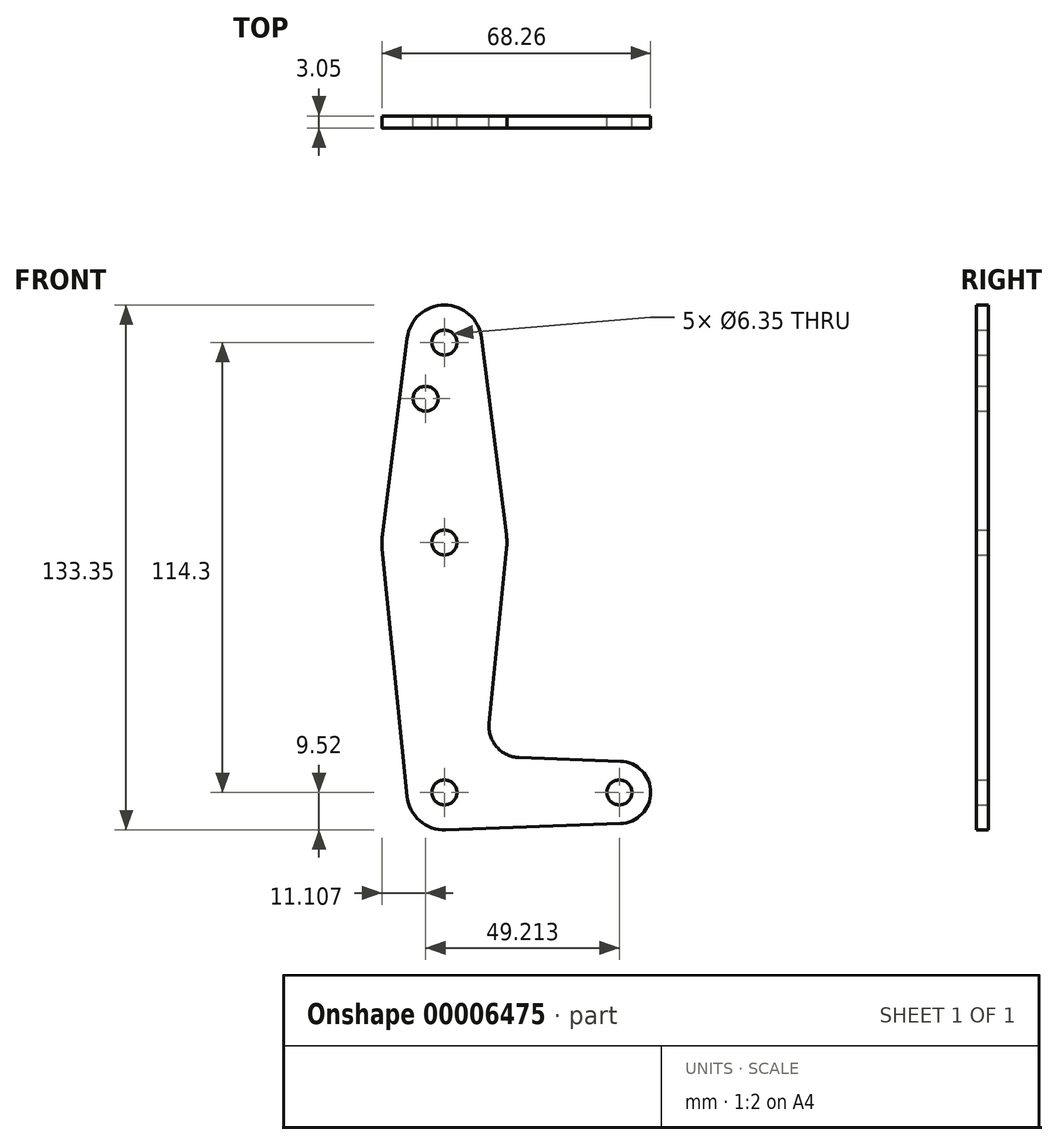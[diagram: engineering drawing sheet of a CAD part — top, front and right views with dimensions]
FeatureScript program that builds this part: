
annotation { "Feature Type Name" : "Feature", "Feature Type Description" : "" }
export const myFeature = defineFeature(function(context is Context, id is Id, definition is map)
    precondition{}
    {
        {
            var Q0;
            Q0=qCreatedBy(makeId("Front.planeOp"),FACE);
            var sketch = newSketch(context, id + "F0", { "sketchPlane" : qUnion([Q0])});
            skLineSegment(sketch, "E0", {"start": v(0, 114.3) * mm, "end": v(0, 0) * mm, "construction": true});
            skLineSegment(sketch, "E1", {"start": v(0, 0) * mm, "end": v(44.45, 0) * mm, "construction": true});
            skCircle(sketch, "E2", {"center": v(0, 0) * mm, "radius": 9.53 * mm});
            skCircle(sketch, "E3", {"center": v(0, 63.5) * mm, "radius": 15.88 * mm});
            skCircle(sketch, "E4", {"center": v(0, 114.3) * mm, "radius": 9.53 * mm});
            skCircle(sketch, "E5", {"center": v(44.45, 0) * mm, "radius": 7.94 * mm});
            skLineSegment(sketch, "E6", {"start": v(-9.45, 115.5) * mm, "end": v(-15.75, 65.48) * mm});
            skLineSegment(sketch, "E7", {"start": v(11.37, 17.59) * mm, "end": v(15.8, 61.92) * mm});
            skLineSegment(sketch, "E8", {"start": v(15.75, 65.48) * mm, "end": v(9.45, 115.5) * mm});
            skLineSegment(sketch, "E9", {"start": v(-15.8, 61.91) * mm, "end": v(-9.48, -0.95) * mm});
            skLineSegment(sketch, "E10", {"start": v(0.34, -9.52) * mm, "end": v(44.73, -7.93) * mm});
            skLineSegment(sketch, "E11", {"start": v(19, 8.85) * mm, "end": v(44.73, 7.93) * mm});
            skCircle(sketch, "E12", {"center": v(-4.76, 100.03) * mm, "radius": 3.18 * mm});
            skCircle(sketch, "E13", {"center": v(0, 63.5) * mm, "radius": 3.18 * mm});
            skCircle(sketch, "E14", {"center": v(0, 0) * mm, "radius": 3.18 * mm});
            skCircle(sketch, "E15", {"center": v(44.45, 0) * mm, "radius": 3.18 * mm});
            skArc(sketch, "E16.filletArc", {"start": v(11.37, 17.59) * mm, "mid": v(13.3, 11.57) * mm, "end": v(19, 8.85) * mm});
            skCircle(sketch, "E17", {"center": v(0, 114.3) * mm, "radius": 3.18 * mm});
            skSolve(sketch);
        }
        {
            var Q0;
            Q0 = qSketchRegion(id + "F0", true);
            extrude(context, id + "F1", {"entities" : qUnion([Q0]), "depth" : 3.05 * mm});
        }
    });
